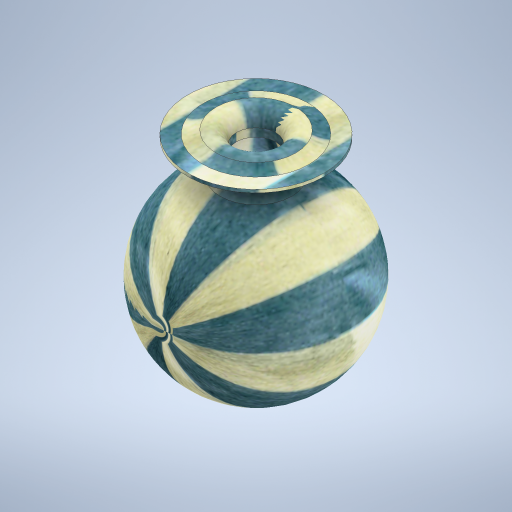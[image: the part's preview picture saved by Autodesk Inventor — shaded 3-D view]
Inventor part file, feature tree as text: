
AUTODESK INVENTOR PART (.ipt)
format: ipt  version: 2023 (Build 270158030, 158C)  size: 539,136 bytes
history: native  units: in
note: dims shown in document units (in); Inventor stores cm internally (conversion verified against a paired STEP export)
features: revolve x1, sketch x1
ambient origin geometry x8: Origin, YZ Plane, XZ Plane, XY Plane, X Axis, Y Axis, Z Axis, Center Point
bodies: Solid1 (feature_tree)
feature tree (2):
  revolve  "Revolution1"  Angle=90.0deg
  sketch  "Sketch1"  dims[d0=6.0in d4=90.0deg d8=4.5in d9=0.9in d10=0.1in d11=3.1in d13=1.0in d14=0.45in d15=0.7in d16=1.5in d18=3.5in]
